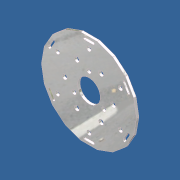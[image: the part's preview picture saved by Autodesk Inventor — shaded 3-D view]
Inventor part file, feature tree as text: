
AUTODESK INVENTOR PART (.ipt)
format: ipt  version: 2011 (Build 150239000, 239)  size: 177,664 bytes
history: native  units: in
note: dims shown in document units (in); Inventor stores cm internally (conversion verified against a paired STEP export)
features: extrude x1, sketch x1
ambient origin geometry x8: Origin, YZ Plane, XZ Plane, XY Plane, X Axis, Y Axis, Z Axis, Center Point
bodies: Solid1 (feature_tree)
feature tree (2):
  extrude  "Extrusion1"  Depth=0.1705in
  sketch  "Sketch1"  dims[d1=0.095in d2=0.335in d7=0.1705in d9=0.192in d11=0.221in d13=0.6625in d14=0.875in d16=1.687in d17=2.3622in d19=360.0deg d23=1.1811in d25=360.0deg d27=2.3622in d29=360.0deg d31=0.095in d32=0.0in d33=3.625in d35=0.335in d36=3.25in]
